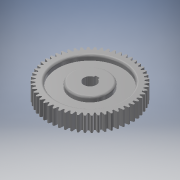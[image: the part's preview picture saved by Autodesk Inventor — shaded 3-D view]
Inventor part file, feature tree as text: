
AUTODESK INVENTOR PART (.ipt)
format: ipt  version: 2018 (Build 220112000, 112)  size: 774,144 bytes
history: native  units: mm (DEFAULTED — no unit token found)
features: sketch x5, extrude x4, plane x4, other x3, mirror x2, projected_geometry x2, fillet x1
ambient origin geometry x8: Origin, YZ Plane, XZ Plane, XY Plane, X Axis, Y Axis, Z Axis, Center Point
bodies: Body1 (feature_tree), Body2 (feature_tree)
feature tree (21):
  extrude  "Extrusion1"  Depth=30.0mm TaperAngle=0.0deg
  plane  "Work Plane2"
  plane  "Work Plane8"
  plane  "Work Plane9"
  other  "Engranaje recto"
  extrude  "Extrusión2"  Depth=10.0mm TaperAngle=0.0deg
  extrude  "Extrusión3"  Depth=0.581776mm TaperAngle=0.0deg
  extrude  "Extrusion4"  TaperAngle=0.0deg  [1 undecoded]
  fillet  "Fillet2"  Radius=108.0mm
  plane  "Work Plane11"
  mirror  "Mirror1"
  mirror  "Mirror2"
  sketch  "Sketch1"  dims[d0=168.0mm d1=30.0mm d2=0.0mm]
  sketch  "Sketch2"  dims[d3=162.0mm d4=10.0mm d5=0.0mm]
  other  "Srf1"
  sketch  "Boceto3"  dims[d16=108.0mm d17=0.0mm d34=0.581776mm]
  sketch  "Boceto4"  dims[d39=0.0mm d41=0.0mm d43=108.0mm]
  projected_geometry  "Contorno proyectado1"
  sketch  "Sketch5"  dims[d46=108.0mm d47=0.0mm d48=0.0mm d49=25.0mm d50=10.0mm d51=0.0mm d52=8.0mm d53=6.0mm d54=10.0mm d55=0.0mm d56=130.0mm d57=75.0mm d58=10.0mm d59=0.0mm d61=4.0mm]
  projected_geometry  "Projected Loop2"
  other  "Diámetro de separación"
note: 1 required parameter value undecoded (feature->parameter linkage not recoverable at this tier; creation-order binding heuristic only, values carry confidence <= 0.55)
